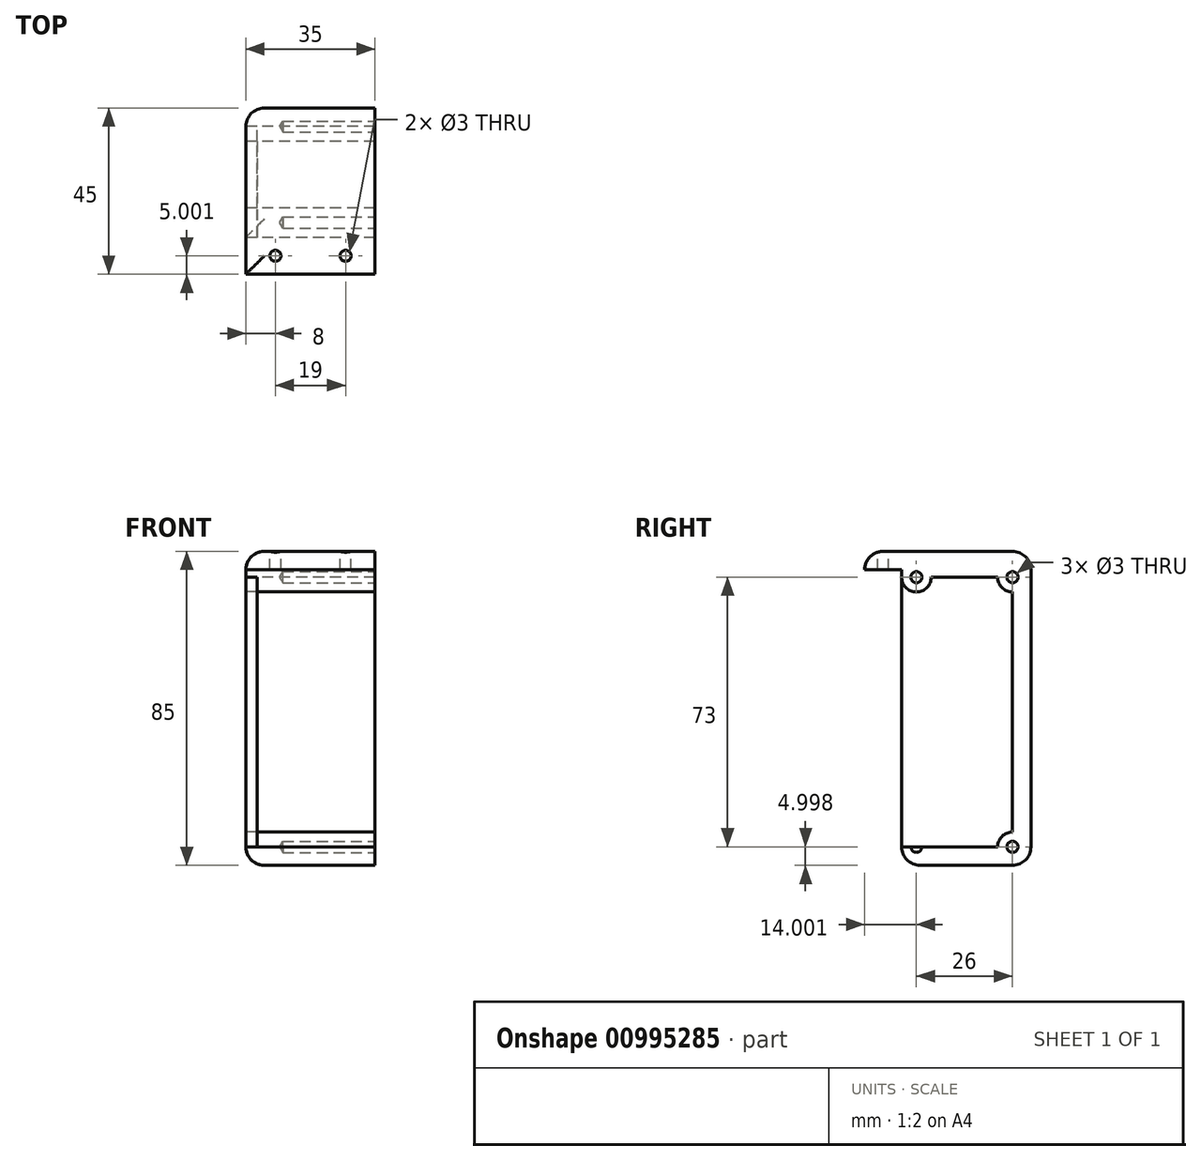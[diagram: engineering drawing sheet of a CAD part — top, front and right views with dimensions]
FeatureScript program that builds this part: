
annotation { "Feature Type Name" : "Feature", "Feature Type Description" : "" }
export const myFeature = defineFeature(function(context is Context, id is Id, definition is map)
    precondition{}
    {
        {
            var Q0;
            Q0=qCreatedBy(makeId("Right.planeOp"),FACE);
            var sketch = newSketch(context, id + "F0", { "sketchPlane" : qUnion([Q0])});
            skLineSegment(sketch, "E0", {"start": v(-2.24, -0.58) * mm, "end": v(7.76, -0.58) * mm});
            skLineSegment(sketch, "E1", {"start": v(7.76, -0.58) * mm, "end": v(7.76, -2.58) * mm});
            skLineSegment(sketch, "E2", {"start": v(7.76, -2.58) * mm, "end": v(37.76, -2.58) * mm});
            skLineSegment(sketch, "E3", {"start": v(37.76, -2.58) * mm, "end": v(37.76, -75.58) * mm});
            skLineSegment(sketch, "E4", {"start": v(37.76, -75.58) * mm, "end": v(7.76, -75.58) * mm});
            skLineSegment(sketch, "E5", {"start": v(7.76, -75.58) * mm, "end": v(7.76, -80.58) * mm});
            skLineSegment(sketch, "E6", {"start": v(7.76, -80.58) * mm, "end": v(42.76, -80.58) * mm});
            skLineSegment(sketch, "E7", {"start": v(42.76, -80.58) * mm, "end": v(42.76, 4.42) * mm});
            skLineSegment(sketch, "E8", {"start": v(42.76, 4.42) * mm, "end": v(-2.24, 4.42) * mm});
            skLineSegment(sketch, "E9", {"start": v(-2.24, 4.42) * mm, "end": v(-2.24, -0.58) * mm});
            skPoint(sketch, "E10", {"position": v(37.76, -39.08) * mm});
            skArc(sketch, "E11", {"start": v(37.76, -71.58) * mm, "mid": v(34.93, -72.75) * mm, "end": v(33.76, -75.58) * mm});
            skArc(sketch, "E12", {"start": v(33.76, -2.58) * mm, "mid": v(34.93, -5.41) * mm, "end": v(37.76, -6.58) * mm});
            skArc(sketch, "E13", {"start": v(7.76, -2.58) * mm, "mid": v(11.76, -6.58) * mm, "end": v(15.76, -2.58) * mm});
            skArc(sketch, "E14", {"start": v(7.76, -75.58) * mm, "mid": v(11.76, -71.58) * mm, "end": v(15.76, -75.58) * mm});
            skSolve(sketch);
        }
        {
            var Q0;
            Q0=makeQuery(id+"F0.imprint","IMPRINT",FACE,{"disambiguationData":[TD([[makeQuery(id+"F0.imprint","IMPRINT",EDGE,{"derivedFrom":sQuery(id+"F0.wireOp",EDGE,"E0")}),1.0]])]});
            var Q1;
            {var subQ0=sQuery(id+"F0.wireOp",EDGE,"E13");Q1=makeQuery(id+"F0.imprint","IMPRINT",FACE,{"disambiguationData":[TD([[makeQuery(id+"F0.imprint","IMPRINT",EDGE,{"derivedFrom":subQ0}),1.0]])]});}
            var Q2;
            {var subQ0=sQuery(id+"F0.wireOp",EDGE,"E12");Q2=makeQuery(id+"F0.imprint","IMPRINT",FACE,{"disambiguationData":[TD([[makeQuery(id+"F0.imprint","IMPRINT",EDGE,{"derivedFrom":subQ0}),1.0]])]});}
            var Q3;
            {var subQ0=sQuery(id+"F0.wireOp",EDGE,"E14");Q3=makeQuery(id+"F0.imprint","IMPRINT",FACE,{"disambiguationData":[TD([[makeQuery(id+"F0.imprint","IMPRINT",EDGE,{"derivedFrom":subQ0}),-1.0]])]});}
            var Q4;
            {var subQ0=sQuery(id+"F0.wireOp",EDGE,"E11");Q4=makeQuery(id+"F0.imprint","IMPRINT",FACE,{"disambiguationData":[TD([[makeQuery(id+"F0.imprint","IMPRINT",EDGE,{"derivedFrom":subQ0}),1.0]])]});}
            extrude(context, id + "F1", {"entities" : qUnion([Q0, Q1, Q2, Q3, Q4]), "endBound" : BoundingType.SYMMETRIC, "depth" : 35 * mm, "offsetDistance" : 25 * mm});
        }
        {
            var Q0;
            Q0=makeQuery(id+"F1.opExtrude","CAP_FACE",FACE,{"disambiguationData":[OSD([sQuery(id+"F0.wireOp",EDGE,"E0"),sQuery(id+"F0.wireOp",EDGE,"E1"),sQuery(id+"F0.wireOp",EDGE,"E2"),sQuery(id+"F0.wireOp",EDGE,"E3"),sQuery(id+"F0.wireOp",EDGE,"E4"),sQuery(id+"F0.wireOp",EDGE,"E5"),sQuery(id+"F0.wireOp",EDGE,"E6"),sQuery(id+"F0.wireOp",EDGE,"E7"),sQuery(id+"F0.wireOp",EDGE,"E8"),sQuery(id+"F0.wireOp",EDGE,"E9")])],"isStart":true});
            var sketch = newSketch(context, id + "F2", { "sketchPlane" : qUnion([Q0])});
            skLineSegment(sketch, "E15.bottom", {"start": v(-42.76, 4.42) * mm, "end": v(-7.76, 4.42) * mm});
            skLineSegment(sketch, "E15.top", {"start": v(-42.76, -80.58) * mm, "end": v(-7.76, -80.58) * mm});
            skLineSegment(sketch, "E15.left", {"start": v(-42.76, 4.42) * mm, "end": v(-42.76, -80.58) * mm});
            skLineSegment(sketch, "E15.right", {"start": v(-7.76, 4.42) * mm, "end": v(-7.76, -80.58) * mm});
            skSolve(sketch);
        }
        {
            var Q0;
            {var subQ1=makeQuery(id+"F1.opExtrude","CAP_EDGE",EDGE,{"disambiguationData":[OSD([sQuery(id+"F0.wireOp",EDGE,"E2")])],"isStart":true});Q0=makeQuery(id+"F2.imprint","IMPRINT",FACE,{"disambiguationData":[TD([[makeQuery(id+"F2.imprint","IMPRINT",EDGE,{"derivedFrom":subQ1}),1.0]])]});}
            extrude(context, id + "F3", {"entities" : qUnion([Q0]), "depth" : -3 * mm, "offsetDistance" : 25 * mm});
        }
        {
            var Q0;
            Q0=makeQuery(id+"F1.opExtrude","CAP_FACE",FACE,{"disambiguationData":[OSD([sQuery(id+"F0.wireOp",EDGE,"E0"),sQuery(id+"F0.wireOp",EDGE,"E1"),sQuery(id+"F0.wireOp",EDGE,"E2"),sQuery(id+"F0.wireOp",EDGE,"E3"),sQuery(id+"F0.wireOp",EDGE,"E4"),sQuery(id+"F0.wireOp",EDGE,"E5"),sQuery(id+"F0.wireOp",EDGE,"E6"),sQuery(id+"F0.wireOp",EDGE,"E7"),sQuery(id+"F0.wireOp",EDGE,"E8"),sQuery(id+"F0.wireOp",EDGE,"E9"),sQuery(id+"F0.wireOp",EDGE,"E11"),sQuery(id+"F0.wireOp",EDGE,"E12"),sQuery(id+"F0.wireOp",EDGE,"E13"),sQuery(id+"F0.wireOp",EDGE,"E14")])],"isStart":false});
            var sketch = newSketch(context, id + "F4", { "sketchPlane" : qUnion([Q0])});
            skPoint(sketch, "E16", {"position": v(11.76, -2.58) * mm});
            skPoint(sketch, "E17", {"position": v(37.76, -2.58) * mm});
            skPoint(sketch, "E18", {"position": v(37.76, -75.58) * mm});
            skPoint(sketch, "E19", {"position": v(11.76, -75.58) * mm});
            skSolve(sketch);
        }
        {
            var Q0;
            Q0=sQuery(id+"F4.wireOp",VERTEX,"E16");
            var Q1;
            Q1=sQuery(id+"F4.wireOp",VERTEX,"E17");
            var Q2;
            Q2=sQuery(id+"F4.wireOp",VERTEX,"E18");
            var Q3;
            Q3=sQuery(id+"F4.wireOp",VERTEX,"E19");
            var Q4;
            Q4=makeQuery(id+"F1.opExtrude","SWEPT_BODY",BODY,{"disambiguationData":[OSD([sQuery(id+"F0.wireOp",EDGE,"E0"),sQuery(id+"F0.wireOp",EDGE,"E1"),sQuery(id+"F0.wireOp",EDGE,"E2"),sQuery(id+"F0.wireOp",EDGE,"E3"),sQuery(id+"F0.wireOp",EDGE,"E4"),sQuery(id+"F0.wireOp",EDGE,"E5"),sQuery(id+"F0.wireOp",EDGE,"E6"),sQuery(id+"F0.wireOp",EDGE,"E7"),sQuery(id+"F0.wireOp",EDGE,"E8"),sQuery(id+"F0.wireOp",EDGE,"E9"),sQuery(id+"F0.wireOp",EDGE,"E11"),sQuery(id+"F0.wireOp",EDGE,"E12"),sQuery(id+"F0.wireOp",EDGE,"E13"),sQuery(id+"F0.wireOp",EDGE,"E14")])]});
            hole(context, id + "F5", {"style" : HoleStyle.SIMPLE, "endStyle" : HoleEndStyle.BLIND, "holeDiameter" : 3 * mm, "majorDiameter" : 5 * mm, "holeDepth" : 25 * mm, "isTappedThrough" : true, "tappedDepth" : 12 * mm, "tapClearance" : 3, "locations" : qUnion([Q0, Q1, Q2, Q3]), "scope" : qUnion([Q4])});
        }
        {
            var Q0;
            Q0=makeQuery(id+"F1.opExtrude","SWEPT_FACE",FACE,{"disambiguationData":[OSD([sQuery(id+"F0.wireOp",EDGE,"E8")])]});
            var sketch = newSketch(context, id + "F6", { "sketchPlane" : qUnion([Q0])});
            skPoint(sketch, "E20", {"position": v(-9.5, 2.76) * mm});
            skPoint(sketch, "E21", {"position": v(9.5, 2.76) * mm});
            skLineSegment(sketch, "E22", {"start": v(-9.5, 2.76) * mm, "end": v(9.5, 2.76) * mm, "construction": true});
            skLineSegment(sketch, "E23", {"start": v(-17.5, 2.76) * mm, "end": v(-9.5, 2.76) * mm, "construction": true});
            skLineSegment(sketch, "E24", {"start": v(-9.5, 2.76) * mm, "end": v(-9.5, -2.24) * mm, "construction": true});
            skLineSegment(sketch, "E25", {"start": v(9.5, 2.76) * mm, "end": v(17.5, 2.76) * mm, "construction": true});
            skSolve(sketch);
        }
        {
            var Q0;
            Q0=sQuery(id+"F6.wireOp",VERTEX,"E20");
            var Q1;
            Q1=sQuery(id+"F6.wireOp",VERTEX,"E21");
            var Q2;
            Q2=makeQuery(id+"F1.opExtrude","SWEPT_BODY",BODY,{"disambiguationData":[OSD([sQuery(id+"F0.wireOp",EDGE,"E0"),sQuery(id+"F0.wireOp",EDGE,"E1"),sQuery(id+"F0.wireOp",EDGE,"E2"),sQuery(id+"F0.wireOp",EDGE,"E3"),sQuery(id+"F0.wireOp",EDGE,"E4"),sQuery(id+"F0.wireOp",EDGE,"E5"),sQuery(id+"F0.wireOp",EDGE,"E6"),sQuery(id+"F0.wireOp",EDGE,"E7"),sQuery(id+"F0.wireOp",EDGE,"E8"),sQuery(id+"F0.wireOp",EDGE,"E9"),sQuery(id+"F0.wireOp",EDGE,"E11"),sQuery(id+"F0.wireOp",EDGE,"E12"),sQuery(id+"F0.wireOp",EDGE,"E13"),sQuery(id+"F0.wireOp",EDGE,"E14")])]});
            hole(context, id + "F7", {"style" : HoleStyle.SIMPLE, "endStyle" : HoleEndStyle.BLIND, "holeDiameter" : 3 * mm, "majorDiameter" : 5 * mm, "holeDepth" : 25 * mm, "isTappedThrough" : true, "tappedDepth" : 12 * mm, "tapClearance" : 3, "locations" : qUnion([Q0, Q1]), "scope" : qUnion([Q2])});
        }
        {
            var Q0;
            Q0=makeQuery(id+"F1.opExtrude","SWEPT_EDGE",EDGE,{"disambiguationData":[OSD([sQuery(id+"F0.wireOp",EDGE,"E8"),sQuery(id+"F0.wireOp",EDGE,"E9")])]});
            var Q1;
            Q1=makeQuery(id+"F1.opExtrude","SWEPT_EDGE",EDGE,{"disambiguationData":[OSD([sQuery(id+"F0.wireOp",EDGE,"E7"),sQuery(id+"F0.wireOp",EDGE,"E8")])]});
            var Q2;
            Q2=makeQuery(id+"F1.opExtrude","SWEPT_EDGE",EDGE,{"disambiguationData":[OSD([sQuery(id+"F0.wireOp",EDGE,"E6"),sQuery(id+"F0.wireOp",EDGE,"E7")])]});
            var Q3;
            Q3=makeQuery(id+"F1.opExtrude","SWEPT_EDGE",EDGE,{"disambiguationData":[OSD([sQuery(id+"F0.wireOp",EDGE,"E5"),sQuery(id+"F0.wireOp",EDGE,"E6")])]});
            var Q4;
            Q4=makeQuery(id+"F1.opExtrude","CAP_EDGE",EDGE,{"disambiguationData":[OSD([sQuery(id+"F0.wireOp",EDGE,"E7")])],"isStart":true});
            var Q5;
            Q5=makeQuery(id+"F1.opExtrude","CAP_EDGE",EDGE,{"disambiguationData":[OSD([sQuery(id+"F0.wireOp",EDGE,"E6")])],"isStart":true});
            var Q6;
            Q6=makeQuery(id+"F1.opExtrude","CAP_EDGE",EDGE,{"disambiguationData":[OSD([sQuery(id+"F0.wireOp",EDGE,"E8")])],"isStart":true});
            fillet(context, id + "F8", {"entities" : qUnion([Q0, Q1, Q2, Q3, Q4, Q5, Q6]), "radius" : 5 * mm, "tangentPropagation" : true, "allowEdgeOverflow" : false});
        }
    });
